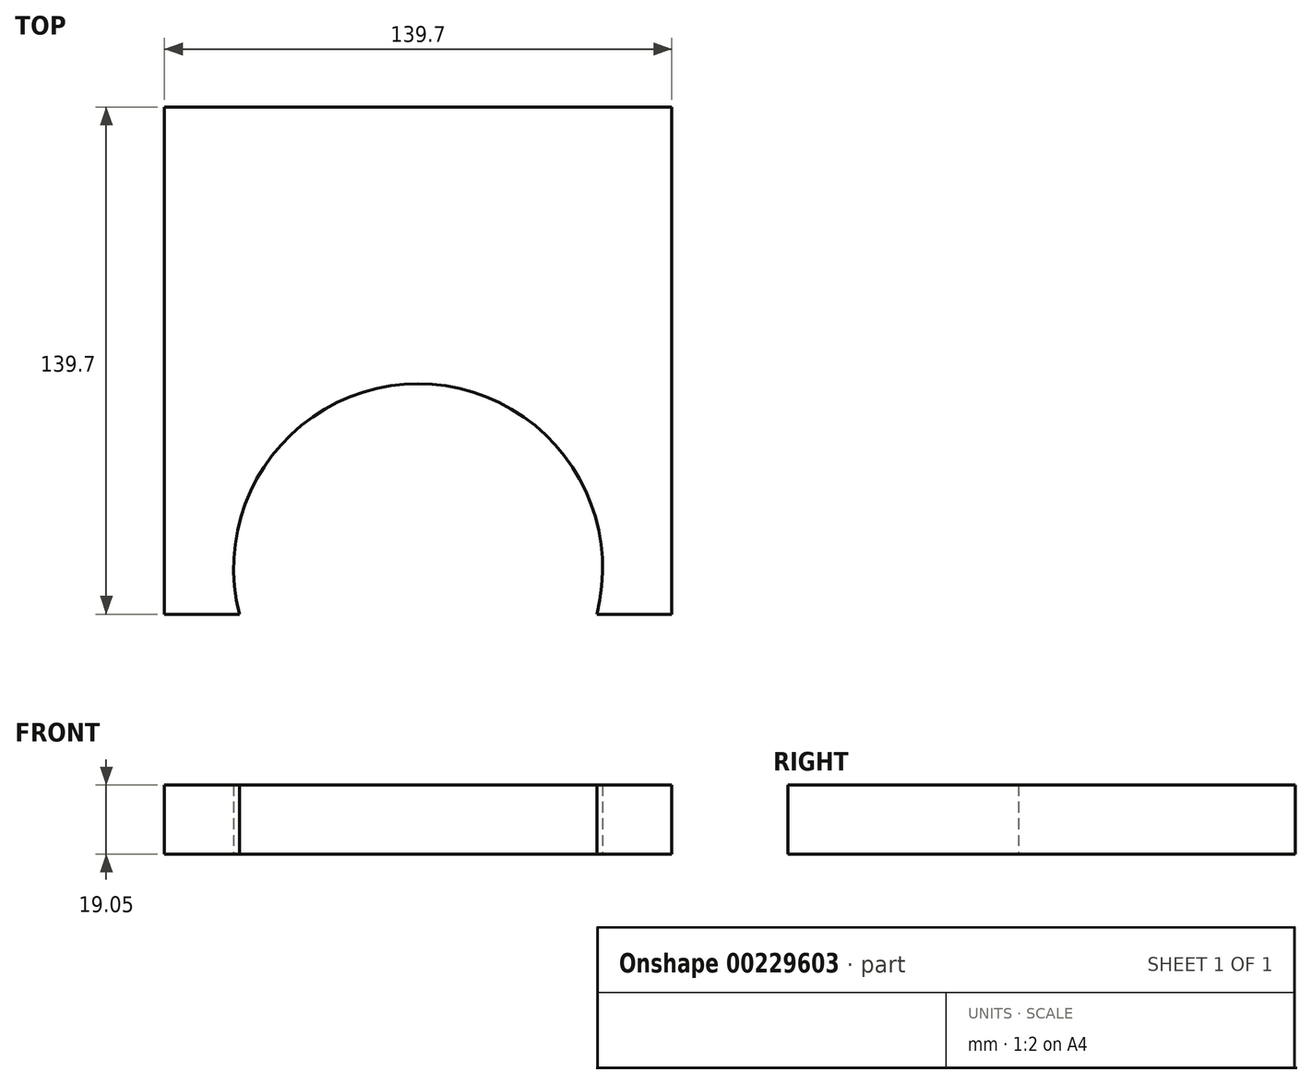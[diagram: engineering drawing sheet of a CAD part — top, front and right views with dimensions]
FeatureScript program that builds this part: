
annotation { "Feature Type Name" : "Feature", "Feature Type Description" : "" }
export const myFeature = defineFeature(function(context is Context, id is Id, definition is map)
    precondition{}
    {
        {
            var Q0;
            Q0=qCreatedBy(makeId("Top.planeOp"),FACE);
            var sketch = newSketch(context, id + "F0", { "sketchPlane" : qUnion([Q0])});
            skLineSegment(sketch, "E0.bottom", {"start": v(69.85, -69.85) * mm, "end": v(49.19, -69.85) * mm});
            skLineSegment(sketch, "E0.top", {"start": v(69.85, 69.85) * mm, "end": v(-69.85, 69.85) * mm});
            skLineSegment(sketch, "E0.left", {"start": v(69.85, -69.85) * mm, "end": v(69.85, 69.85) * mm});
            skLineSegment(sketch, "E0.right", {"start": v(-69.85, -69.85) * mm, "end": v(-69.85, 69.85) * mm});
            skPoint(sketch, "E0.middle", {"position": v(0, 0) * mm});
            skArc(sketch, "E1", {"start": v(49.19, -69.85) * mm, "mid": v(0, -6.35) * mm, "end": v(-49.19, -69.85) * mm});
            skPoint(sketch, "E2.start.orphan", {"position": v(0, -69.85) * mm});
            skLineSegment(sketch, "E3.trimOffspring", {"start": v(-49.19, -69.85) * mm, "end": v(-69.85, -69.85) * mm});
            skSolve(sketch);
        }
        {
            var Q0;
            Q0 = qSketchRegion(id + "F0", true);
            extrude(context, id + "F1", {"entities" : qUnion([Q0]), "depth" : 19.05 * mm});
        }
    });
